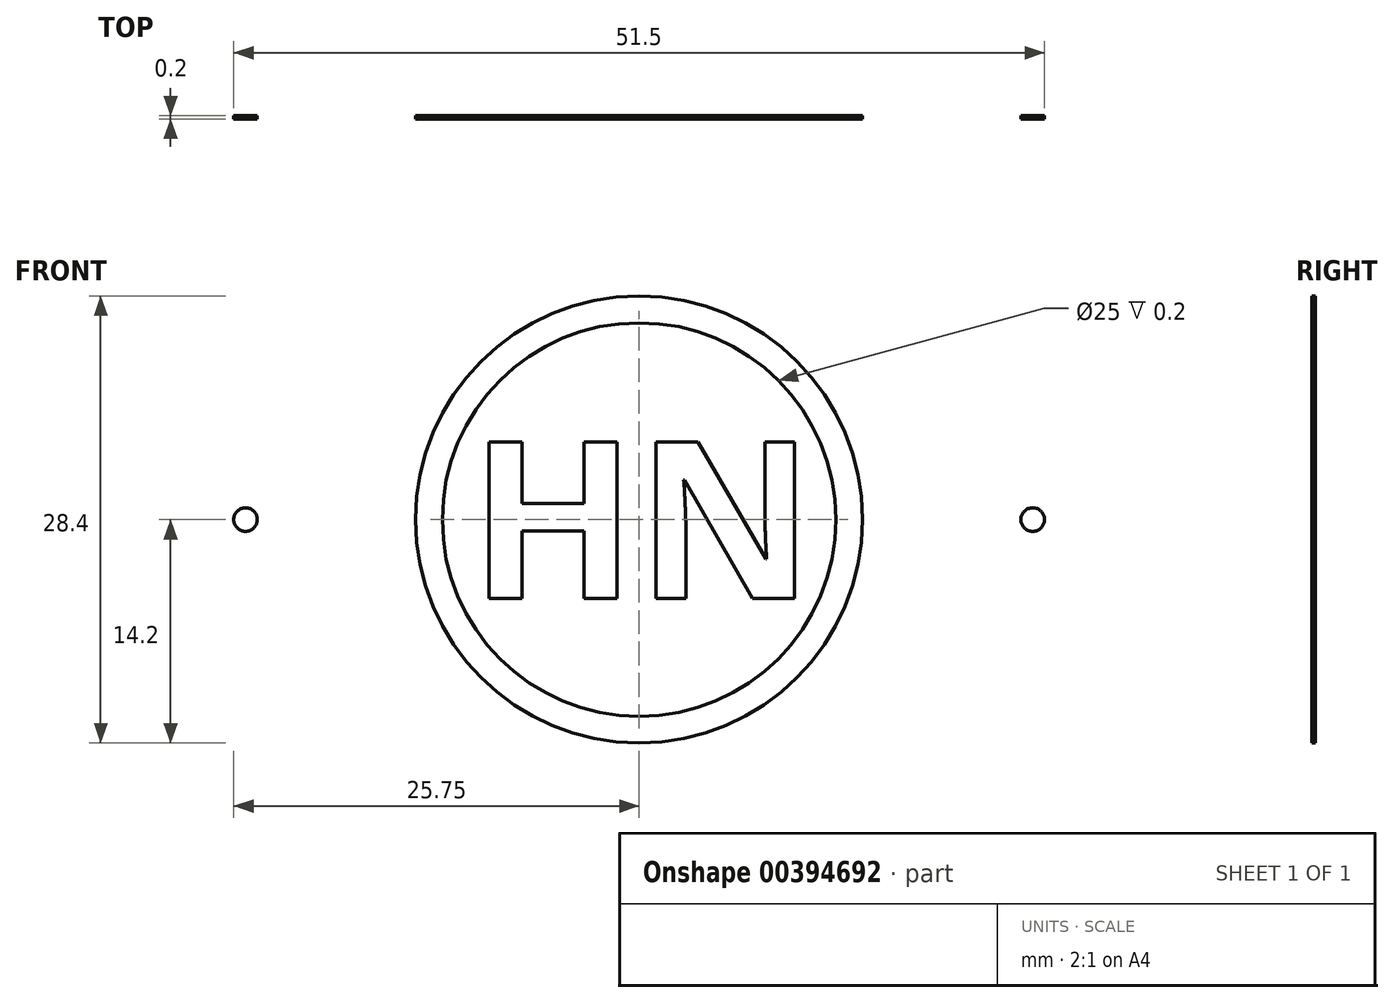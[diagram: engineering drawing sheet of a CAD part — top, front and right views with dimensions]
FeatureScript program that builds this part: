
annotation { "Feature Type Name" : "Feature", "Feature Type Description" : "" }
export const myFeature = defineFeature(function(context is Context, id is Id, definition is map)
    precondition{}
    {
        {
            var Q0;
            Q0=qCreatedBy(makeId("Front.planeOp"),FACE);
            var sketch = newSketch(context, id + "F0", { "sketchPlane" : qUnion([Q0])});
            skCircle(sketch, "E0", {"center": v(0, 0) * mm, "radius": 17.5 * mm});
            skSolve(sketch);
        }
        {
            var Q0;
            Q0=qSketchRegion(id+"F0",true);
            extrude(context, id + "F1", {"entities" : qUnion([Q0]), "depth" : 1 * mm});
        }
        {
            var Q0;
            Q0=makeQuery(id+"F1.opExtrude","CAP_FACE",FACE,{"disambiguationData":[OSD([sQuery(id+"F0.wireOp",EDGE,"E0")])],"isStart":true});
            var sketch = newSketch(context, id + "F2", { "sketchPlane" : qUnion([Q0])});
            skCircle(sketch, "E1", {"center": v(0, 0) * mm, "radius": 17.5 * mm});
            skCircle(sketch, "E2", {"center": v(0, 0) * mm, "radius": 15.25 * mm});
            skSolve(sketch);
        }
        {
            var Q0;
            Q0=qSketchRegion(id+"F2",true);
            extrude(context, id + "F3", {"entities" : qUnion([Q0]), "operationType" : NewBodyOperationType.ADD, "depth" : 1 * mm});
        }
        {
            var Q0;
            Q0=makeQuery(id+"F3.opExtrude","CAP_FACE",FACE,{"disambiguationData":[OSD([sQuery(id+"F2.wireOp",EDGE,"E1"),sQuery(id+"F2.wireOp",EDGE,"E2")])],"isStart":false});
            var sketch = newSketch(context, id + "F4", { "sketchPlane" : qUnion([Q0])});
            skCircle(sketch, "E3", {"center": v(0, 0) * mm, "radius": 17.5 * mm});
            skSolve(sketch);
        }
        {
            var Q0;
            Q0=qSketchRegion(id+"F4",true);
            extrude(context, id + "F5", {"entities" : qUnion([Q0]), "operationType" : NewBodyOperationType.ADD, "depth" : 1 * mm});
        }
        {
            var Q0;
            Q0=makeQuery(id+"F1.opExtrude","CAP_FACE",FACE,{"disambiguationData":[OSD([sQuery(id+"F0.wireOp",EDGE,"E0")])],"isStart":false});
            var sketch = newSketch(context, id + "F6", { "sketchPlane" : qUnion([Q0])});
            skText(sketch, "E4", { "text": "HN", "fontName": "OpenSans-Bold.ttf"});
            skCircle(sketch, "E5", {"center": v(0, 0) * mm, "radius": 12.5 * mm});
            skCircle(sketch, "E6", {"center": v(0, 0) * mm, "radius": 14.2 * mm});
            const initialGuessF6  = {"E4": [-0.01079, -0.005, 1, 0, 0.01]};
            skSetInitialGuess(sketch, initialGuessF6);
            skSolve(sketch);
        }
        {
            var Q0;
            Q0=makeQuery(id+"F6.imprint","IMPRINT",FACE,{"disambiguationData":[TD([[makeQuery(id+"F6.imprint","IMPRINT",EDGE,{"derivedFrom":sQuery(id+"F6.wireOp",EDGE,"E5")}),-1.0]])]});
            var Q1;
            Q1=makeQuery(id+"F6.imprint","IMPRINT",FACE,{"disambiguationData":[TD([[makeQuery(id+"F6.imprint","IMPRINT",EDGE,{"derivedFrom":sQuery(id+"F6.wireOp",EDGE,"E4.sketch_text.stroke-0")}),-1.0]])]});
            var Q2;
            Q2=makeQuery(id+"F6.imprint","IMPRINT",FACE,{"disambiguationData":[TD([[makeQuery(id+"F6.imprint","IMPRINT",EDGE,{"derivedFrom":sQuery(id+"F6.wireOp",EDGE,"E4.sketch_text.stroke-12")}),-1.0]])]});
            var Q3;
            Q3=makeQuery(id+"F6.imprint","IMPRINT",FACE,{"disambiguationData":[TD([[makeQuery(id+"F6.imprint","IMPRINT",EDGE,{"derivedFrom":sQuery(id+"F6.wireOp",EDGE,"E4.sketch_text.stroke-20")}),-1.0]])]});
            var Q4;
            Q4=makeQuery(id+"F6.imprint","IMPRINT",FACE,{"disambiguationData":[TD([[makeQuery(id+"F6.imprint","IMPRINT",EDGE,{"derivedFrom":sQuery(id+"F6.wireOp",EDGE,"E4.sketch_text.stroke-34")}),-1.0]])]});
            var Q5;
            Q5=makeQuery(id+"F6.imprint","IMPRINT",FACE,{"disambiguationData":[TD([[makeQuery(id+"F6.imprint","IMPRINT",EDGE,{"derivedFrom":sQuery(id+"F6.wireOp",EDGE,"2f791306-b3d7-45ab-86ae-8695a74e6aea.sketch_text.stroke-0")}),-1.0]])]});
            var Q6;
            Q6=makeQuery(id+"F6.imprint","IMPRINT",FACE,{"disambiguationData":[TD([[makeQuery(id+"F6.imprint","IMPRINT",EDGE,{"derivedFrom":sQuery(id+"F6.wireOp",EDGE,"2f791306-b3d7-45ab-86ae-8695a74e6aea.sketch_text.stroke-10")}),-1.0]])]});
            var Q7;
            Q7=makeQuery(id+"F6.imprint","IMPRINT",FACE,{"disambiguationData":[TD([[makeQuery(id+"F6.imprint","IMPRINT",EDGE,{"derivedFrom":sQuery(id+"F6.wireOp",EDGE,"2f791306-b3d7-45ab-86ae-8695a74e6aea.sketch_text.stroke-14")}),-1.0]])]});
            var Q8;
            Q8=makeQuery(id+"F6.imprint","IMPRINT",FACE,{"disambiguationData":[TD([[makeQuery(id+"F6.imprint","IMPRINT",EDGE,{"derivedFrom":sQuery(id+"F6.wireOp",EDGE,"2f791306-b3d7-45ab-86ae-8695a74e6aea.sketch_text.stroke-30")}),-1.0]])]});
            extrude(context, id + "F7", {"entities" : qUnion([Q0, Q1, Q2, Q3, Q4, Q5, Q6, Q7, Q8]), "operationType" : NewBodyOperationType.REMOVE, "oppositeDirection" : true, "depth" : 0.2 * mm});
        }
        {
            var Q0;
            Q0=makeQuery(id+"F7.boolean.opBoolean","COPY",FACE,{"derivedFrom":makeQuery(id+"F7.opExtrude","CAP_FACE",FACE,{"disambiguationData":[OSD([sQuery(id+"F6.wireOp",EDGE,"E5"),sQuery(id+"F6.wireOp",EDGE,"E6")])],"isStart":false})});
            var sketch = newSketch(context, id + "F8", { "sketchPlane" : qUnion([Q0])});
            skCircle(sketch, "E7", {"center": v(0, 0) * mm, "radius": 16.5 * mm});
            skCircle(sketch, "E8", {"center": v(0, 0) * mm, "radius": 15 * mm});
            skText(sketch, "E9", { "text": "VIP", "fontName": "OpenSans-Bold.ttf"});
            skText(sketch, "E10", { "text": "H.N.", "fontName": "OpenSans-Bold.ttf"});
            const initialGuessF8  = {"E9": [-0.00735, 0.0025, 1, 0, 0.0065], "E10": [-0.00973, -0.009, 1, 0, 0.0065]};
            skSetInitialGuess(sketch, initialGuessF8);
            skSolve(sketch);
        }
        {
            var Q0;
            Q0=makeQuery(id+"F8.imprint","IMPRINT",FACE,{"disambiguationData":[TD([[makeQuery(id+"F8.imprint","IMPRINT",EDGE,{"derivedFrom":sQuery(id+"F8.wireOp",EDGE,"E9.sketch_text.stroke-0")}),-1.0]])]});
            var Q1;
            Q1=makeQuery(id+"F8.imprint","IMPRINT",FACE,{"disambiguationData":[TD([[makeQuery(id+"F8.imprint","IMPRINT",EDGE,{"derivedFrom":sQuery(id+"F8.wireOp",EDGE,"E9.sketch_text.stroke-10")}),-1.0]])]});
            var Q2;
            Q2=makeQuery(id+"F8.imprint","IMPRINT",FACE,{"disambiguationData":[TD([[makeQuery(id+"F8.imprint","IMPRINT",EDGE,{"derivedFrom":sQuery(id+"F8.wireOp",EDGE,"E9.sketch_text.stroke-14")}),-1.0]])]});
            var Q3;
            Q3=makeQuery(id+"F8.imprint","IMPRINT",FACE,{"disambiguationData":[TD([[makeQuery(id+"F8.imprint","IMPRINT",EDGE,{"derivedFrom":sQuery(id+"F8.wireOp",EDGE,"E9.sketch_text.stroke-30")}),-1.0]])]});
            var Q4;
            Q4=makeQuery(id+"F8.imprint","IMPRINT",FACE,{"disambiguationData":[TD([[makeQuery(id+"F8.imprint","IMPRINT",EDGE,{"derivedFrom":sQuery(id+"F8.wireOp",EDGE,"E10.sketch_text.stroke-0")}),-1.0]])]});
            var Q5;
            Q5=makeQuery(id+"F8.imprint","IMPRINT",FACE,{"disambiguationData":[TD([[makeQuery(id+"F8.imprint","IMPRINT",EDGE,{"derivedFrom":sQuery(id+"F8.wireOp",EDGE,"E10.sketch_text.stroke-12")}),-1.0]])]});
            var Q6;
            Q6=makeQuery(id+"F8.imprint","IMPRINT",FACE,{"disambiguationData":[TD([[makeQuery(id+"F8.imprint","IMPRINT",EDGE,{"derivedFrom":sQuery(id+"F8.wireOp",EDGE,"E10.sketch_text.stroke-20")}),-1.0]])]});
            var Q7;
            Q7=makeQuery(id+"F8.imprint","IMPRINT",FACE,{"disambiguationData":[TD([[makeQuery(id+"F8.imprint","IMPRINT",EDGE,{"derivedFrom":sQuery(id+"F8.wireOp",EDGE,"E10.sketch_text.stroke-34")}),-1.0]])]});
            var Q8;
            Q8=makeQuery(id+"F8.imprint","IMPRINT",FACE,{"disambiguationData":[TD([[makeQuery(id+"F8.imprint","IMPRINT",EDGE,{"derivedFrom":sQuery(id+"F8.wireOp",EDGE,"E7")}),1.0]])]});
            extrude(context, id + "F9", {"entities" : qUnion([Q0, Q1, Q2, Q3, Q4, Q5, Q6, Q7, Q8]), "depth" : 0.2 * mm});
        }
        {
            var Q0;
            Q0=makeQuery(id+"Fh8yMcBjIkPt4Dr_11.boolean.opBoolean","MERGE",FACE,{"derivedFrom":[makeQuery(id+"F5.opExtrude","CAP_FACE",FACE,{"disambiguationData":[OSD([sQuery(id+"F4.wireOp",EDGE,"E3")])],"isStart":false}),makeQuery(id+"Fh8yMcBjIkPt4Dr_11.opExtrude","CAP_FACE",FACE,{"disambiguationData":[OSD([sQuery(id+"FN8h1bw3wlibMYA_11.wireOp",EDGE,"BS7OUwbq-2ru2-1JD7-GIha-xYvTOZTgPK9A"),sQuery(id+"FN8h1bw3wlibMYA_11.wireOp",EDGE,"aJaIA7Kc-m8c6-AEcG-Va6J-VanrhZFaR41i")])],"isStart":false})]});
            var sketch = newSketch(context, id + "F10", { "sketchPlane" : qUnion([Q0])});
            skArc(sketch, "E11", {"start": v(12.63, -6.5) * mm, "mid": v(14.2, -0.52) * mm, "end": v(13.07, 5.55) * mm});
            skLineSegment(sketch, "E12", {"start": v(12.63, -6.5) * mm, "end": v(-4.7, 4) * mm});
            skLineSegment(sketch, "E13", {"start": v(-4.7, 4) * mm, "end": v(-4.7, 2.5) * mm});
            skLineSegment(sketch, "E14", {"start": v(-4.7, 2.5) * mm, "end": v(12.49, -6.76) * mm});
            skLineSegment(sketch, "E15", {"start": v(-4.7, 1.9) * mm, "end": v(-4.7, 0.4) * mm});
            skLineSegment(sketch, "E16", {"start": v(-4.7, 0.4) * mm, "end": v(11.53, -8.28) * mm});
            skLineSegment(sketch, "E17", {"start": v(11.7, -8.04) * mm, "end": v(-4.7, 1.9) * mm});
            skLineSegment(sketch, "E18", {"start": v(-4.7, -0.2) * mm, "end": v(-4.7, -1.7) * mm});
            skLineSegment(sketch, "E19", {"start": v(-4.7, -1.7) * mm, "end": v(10.39, -9.68) * mm});
            skLineSegment(sketch, "E20", {"start": v(10.6, -9.46) * mm, "end": v(-4.7, -0.2) * mm});
            skLineSegment(sketch, "E21", {"start": v(-4.7, -2.3) * mm, "end": v(-4.7, -3.8) * mm});
            skLineSegment(sketch, "E22", {"start": v(-4.7, -3.8) * mm, "end": v(9.04, -10.95) * mm});
            skLineSegment(sketch, "E23", {"start": v(9.27, -10.76) * mm, "end": v(-4.7, -2.3) * mm});
            skLineSegment(sketch, "E24", {"start": v(-4.7, -4.4) * mm, "end": v(-4.7, -5.9) * mm});
            skLineSegment(sketch, "E25", {"start": v(-4.7, -5.9) * mm, "end": v(7.46, -12.08) * mm});
            skLineSegment(sketch, "E26", {"start": v(7.72, -11.92) * mm, "end": v(-4.7, -4.4) * mm});
            skArc(sketch, "E27.trimOffspring", {"start": v(11.7, -8.04) * mm, "mid": v(12.11, -7.4) * mm, "end": v(12.49, -6.76) * mm});
            skArc(sketch, "E28.trimOffspring", {"start": v(10.6, -9.46) * mm, "mid": v(11.08, -8.88) * mm, "end": v(11.53, -8.28) * mm});
            skArc(sketch, "E29.trimOffspring", {"start": v(9.27, -10.76) * mm, "mid": v(9.84, -10.24) * mm, "end": v(10.39, -9.68) * mm});
            skArc(sketch, "E30.trimOffspring", {"start": v(7.72, -11.92) * mm, "mid": v(8.4, -11.46) * mm, "end": v(9.04, -10.95) * mm});
            skLineSegment(sketch, "E31", {"start": v(7.07, 12.32) * mm, "end": v(-4.2, 4.28) * mm});
            skLineSegment(sketch, "E32", {"start": v(-4.2, 4.28) * mm, "end": v(8.2, 11.59) * mm});
            skLineSegment(sketch, "E33", {"start": v(8.69, 11.23) * mm, "end": v(-2.5, 3.25) * mm});
            skLineSegment(sketch, "E34", {"start": v(-2.5, 3.25) * mm, "end": v(9.66, 10.4) * mm});
            skLineSegment(sketch, "E35", {"start": v(10.1, 10) * mm, "end": v(-0.8, 2.22) * mm});
            skLineSegment(sketch, "E36", {"start": v(11.3, 8.6) * mm, "end": v(0.9, 1.2) * mm});
            skLineSegment(sketch, "E37", {"start": v(0.9, 1.2) * mm, "end": v(12, 7.6) * mm});
            skLineSegment(sketch, "E38", {"start": v(12.3, 7.09) * mm, "end": v(2.6, 0.16) * mm});
            skLineSegment(sketch, "E39", {"start": v(2.6, 0.16) * mm, "end": v(13.07, 5.55) * mm});
            skArc(sketch, "E40.trimOffspring", {"start": v(7.07, 12.32) * mm, "mid": v(-14.2, -0.23) * mm, "end": v(7.46, -12.08) * mm});
            skArc(sketch, "E41.trimOffspring", {"start": v(8.69, 11.23) * mm, "mid": v(8.45, 11.41) * mm, "end": v(8.2, 11.59) * mm});
            skArc(sketch, "E42.trimOffspring", {"start": v(10.1, 10) * mm, "mid": v(9.88, 10.2) * mm, "end": v(9.66, 10.4) * mm});
            skArc(sketch, "E43.trimOffspring", {"start": v(11.3, 8.6) * mm, "mid": v(11.1, 8.84) * mm, "end": v(10.92, 9.08) * mm});
            skArc(sketch, "E44.trimOffspring", {"start": v(12.3, 7.09) * mm, "mid": v(12.15, 7.34) * mm, "end": v(12, 7.6) * mm});
            skLineSegment(sketch, "E45", {"start": v(10.92, 9.08) * mm, "end": v(-0.8, 2.22) * mm});
            skSolve(sketch);
        }
        {
            var Q0;
            Q0=qSketchRegion(id+"F10",true);
            extrude(context, id + "F11", {"entities" : qUnion([Q0]), "operationType" : NewBodyOperationType.ADD, "depth" : 0.4 * mm});
        }
        {
            var Q0;
            Q0=makeQuery(id+"F9.opExtrude","SWEPT_BODY",BODY,{"disambiguationData":[OSD([sQuery(id+"F8.wireOp",EDGE,"E7"),sQuery(id+"F8.wireOp",EDGE,"E8")])]});
            var Q1;
            Q1=makeQuery(id+"F9.opExtrude","SWEPT_BODY",BODY,{"disambiguationData":[OSD([sQuery(id+"F8.wireOp",EDGE,"E9.sketch_text.stroke-0"),sQuery(id+"F8.wireOp",EDGE,"E9.sketch_text.stroke-1"),sQuery(id+"F8.wireOp",EDGE,"E9.sketch_text.stroke-2"),sQuery(id+"F8.wireOp",EDGE,"E9.sketch_text.stroke-3"),sQuery(id+"F8.wireOp",EDGE,"E9.sketch_text.stroke-4"),sQuery(id+"F8.wireOp",EDGE,"E9.sketch_text.stroke-5"),sQuery(id+"F8.wireOp",EDGE,"E9.sketch_text.stroke-6"),sQuery(id+"F8.wireOp",EDGE,"E9.sketch_text.stroke-7"),sQuery(id+"F8.wireOp",EDGE,"E9.sketch_text.stroke-8"),sQuery(id+"F8.wireOp",EDGE,"E9.sketch_text.stroke-9")])]});
            var Q2;
            Q2=makeQuery(id+"F9.opExtrude","SWEPT_BODY",BODY,{"disambiguationData":[OSD([sQuery(id+"F8.wireOp",EDGE,"E9.sketch_text.stroke-14"),sQuery(id+"F8.wireOp",EDGE,"E9.sketch_text.stroke-15"),sQuery(id+"F8.wireOp",EDGE,"E9.sketch_text.stroke-16"),sQuery(id+"F8.wireOp",EDGE,"E9.sketch_text.stroke-17"),sQuery(id+"F8.wireOp",EDGE,"E9.sketch_text.stroke-18"),sQuery(id+"F8.wireOp",EDGE,"E9.sketch_text.stroke-19"),sQuery(id+"F8.wireOp",EDGE,"E9.sketch_text.stroke-20"),sQuery(id+"F8.wireOp",EDGE,"E9.sketch_text.stroke-21"),sQuery(id+"F8.wireOp",EDGE,"E9.sketch_text.stroke-22"),sQuery(id+"F8.wireOp",EDGE,"E9.sketch_text.stroke-23"),sQuery(id+"F8.wireOp",EDGE,"E9.sketch_text.stroke-24"),sQuery(id+"F8.wireOp",EDGE,"E9.sketch_text.stroke-25"),sQuery(id+"F8.wireOp",EDGE,"E9.sketch_text.stroke-26"),sQuery(id+"F8.wireOp",EDGE,"E9.sketch_text.stroke-27"),sQuery(id+"F8.wireOp",EDGE,"E9.sketch_text.stroke-28"),sQuery(id+"F8.wireOp",EDGE,"E9.sketch_text.stroke-29")])]});
            var Q3;
            Q3=makeQuery(id+"F9.opExtrude","SWEPT_BODY",BODY,{"disambiguationData":[OSD([sQuery(id+"F8.wireOp",EDGE,"E10.sketch_text.stroke-34"),sQuery(id+"F8.wireOp",EDGE,"E10.sketch_text.stroke-35"),sQuery(id+"F8.wireOp",EDGE,"E10.sketch_text.stroke-36"),sQuery(id+"F8.wireOp",EDGE,"E10.sketch_text.stroke-37"),sQuery(id+"F8.wireOp",EDGE,"E10.sketch_text.stroke-38"),sQuery(id+"F8.wireOp",EDGE,"E10.sketch_text.stroke-39"),sQuery(id+"F8.wireOp",EDGE,"E10.sketch_text.stroke-40"),sQuery(id+"F8.wireOp",EDGE,"E10.sketch_text.stroke-41")])]});
            var Q4;
            Q4=makeQuery(id+"F9.opExtrude","SWEPT_BODY",BODY,{"disambiguationData":[OSD([sQuery(id+"F8.wireOp",EDGE,"E10.sketch_text.stroke-0"),sQuery(id+"F8.wireOp",EDGE,"E10.sketch_text.stroke-1"),sQuery(id+"F8.wireOp",EDGE,"E10.sketch_text.stroke-2"),sQuery(id+"F8.wireOp",EDGE,"E10.sketch_text.stroke-3"),sQuery(id+"F8.wireOp",EDGE,"E10.sketch_text.stroke-4"),sQuery(id+"F8.wireOp",EDGE,"E10.sketch_text.stroke-5"),sQuery(id+"F8.wireOp",EDGE,"E10.sketch_text.stroke-6"),sQuery(id+"F8.wireOp",EDGE,"E10.sketch_text.stroke-7"),sQuery(id+"F8.wireOp",EDGE,"E10.sketch_text.stroke-8"),sQuery(id+"F8.wireOp",EDGE,"E10.sketch_text.stroke-9"),sQuery(id+"F8.wireOp",EDGE,"E10.sketch_text.stroke-10"),sQuery(id+"F8.wireOp",EDGE,"E10.sketch_text.stroke-11")])]});
            deleteBodies(context, id + "F12", {"entities" : qUnion([Q0, Q1, Q2, Q3, Q4])});
        }
        {
            var Q0;
            Q0=makeQuery(id+"F9.opExtrude","SWEPT_BODY",BODY,{"disambiguationData":[OSD([sQuery(id+"F8.wireOp",EDGE,"E9.sketch_text.stroke-10"),sQuery(id+"F8.wireOp",EDGE,"E9.sketch_text.stroke-11"),sQuery(id+"F8.wireOp",EDGE,"E9.sketch_text.stroke-12"),sQuery(id+"F8.wireOp",EDGE,"E9.sketch_text.stroke-13")])]});
            var Q1;
            Q1=makeQuery(id+"F9.opExtrude","SWEPT_BODY",BODY,{"disambiguationData":[OSD([sQuery(id+"F8.wireOp",EDGE,"E10.sketch_text.stroke-12"),sQuery(id+"F8.wireOp",EDGE,"E10.sketch_text.stroke-13"),sQuery(id+"F8.wireOp",EDGE,"E10.sketch_text.stroke-14"),sQuery(id+"F8.wireOp",EDGE,"E10.sketch_text.stroke-15"),sQuery(id+"F8.wireOp",EDGE,"E10.sketch_text.stroke-16"),sQuery(id+"F8.wireOp",EDGE,"E10.sketch_text.stroke-17"),sQuery(id+"F8.wireOp",EDGE,"E10.sketch_text.stroke-18"),sQuery(id+"F8.wireOp",EDGE,"E10.sketch_text.stroke-19")])]});
            deleteBodies(context, id + "F13", {"entities" : qUnion([Q0, Q1])});
        }
        {
            var Q0;
            Q0=makeQuery(id+"F9.opExtrude","SWEPT_BODY",BODY,{"disambiguationData":[OSD([sQuery(id+"F8.wireOp",EDGE,"E10.sketch_text.stroke-20"),sQuery(id+"F8.wireOp",EDGE,"E10.sketch_text.stroke-21"),sQuery(id+"F8.wireOp",EDGE,"E10.sketch_text.stroke-22"),sQuery(id+"F8.wireOp",EDGE,"E10.sketch_text.stroke-23"),sQuery(id+"F8.wireOp",EDGE,"E10.sketch_text.stroke-24"),sQuery(id+"F8.wireOp",EDGE,"E10.sketch_text.stroke-25"),sQuery(id+"F8.wireOp",EDGE,"E10.sketch_text.stroke-26"),sQuery(id+"F8.wireOp",EDGE,"E10.sketch_text.stroke-27"),sQuery(id+"F8.wireOp",EDGE,"E10.sketch_text.stroke-28"),sQuery(id+"F8.wireOp",EDGE,"E10.sketch_text.stroke-29"),sQuery(id+"F8.wireOp",EDGE,"E10.sketch_text.stroke-30"),sQuery(id+"F8.wireOp",EDGE,"E10.sketch_text.stroke-31"),sQuery(id+"F8.wireOp",EDGE,"E10.sketch_text.stroke-32"),sQuery(id+"F8.wireOp",EDGE,"E10.sketch_text.stroke-33")])]});
            deleteBodies(context, id + "F14", {"entities" : qUnion([Q0])});
        }
        {
            var Q0;
            {var subQ0=sQuery(id+"F0.wireOp",EDGE,"E0");Q0=makeQuery(id+"F7.boolean.opBoolean","SPLIT",FACE,{"disambiguationData":[TD([makeQuery(id+"F1.opExtrude","SWEPT_FACE",FACE,{"disambiguationData":[OSD([subQ0])]})])],"derivedFrom":makeQuery(id+"F1.opExtrude","CAP_FACE",FACE,{"disambiguationData":[OSD([subQ0])],"isStart":false})});}
            var sketch = newSketch(context, id + "F15", { "sketchPlane" : qUnion([Q0])});
            skCircle(sketch, "E46", {"center": v(0, 19.5) * mm, "radius": 2 * mm});
            skCircle(sketch, "E47", {"center": v(0, 19.5) * mm, "radius": 4 * mm});
            skSolve(sketch);
        }
        {
            var Q0;
            Q0=qSketchRegion(id+"F15",true);
            var Q1;
            Q1=makeQuery(id+"F5.opExtrude","CAP_FACE",FACE,{"disambiguationData":[OSD([sQuery(id+"F4.wireOp",EDGE,"E3")])],"isStart":false});
            extrude(context, id + "F16", {"entities" : qUnion([Q0]), "operationType" : NewBodyOperationType.ADD, "endBound" : BoundingType.UP_TO_SURFACE, "oppositeDirection" : true, "endBoundEntityFace" : qUnion([Q1]), "depth" : 25 * mm});
        }
        {
            var Q0;
            Q0=makeQuery(id+"F16.boolean.opBoolean","INTERSECT",EDGE,{"disambiguationData":[OD(0.0)],"derivedFrom":[makeQuery(id+"F5.boolean.opBoolean","MERGE",FACE,{"derivedFrom":[makeQuery(id+"F3.boolean.opBoolean","MERGE",FACE,{"derivedFrom":[makeQuery(id+"F1.opExtrude","SWEPT_FACE",FACE,{"disambiguationData":[OSD([sQuery(id+"F0.wireOp",EDGE,"E0")])]}),makeQuery(id+"F3.opExtrude","SWEPT_FACE",FACE,{"disambiguationData":[OSD([sQuery(id+"F2.wireOp",EDGE,"E1")])]})]}),makeQuery(id+"F5.opExtrude","SWEPT_FACE",FACE,{"disambiguationData":[OSD([sQuery(id+"F4.wireOp",EDGE,"E3")])]})]}),makeQuery(id+"F16.opExtrude","SWEPT_FACE",FACE,{"disambiguationData":[OSD([sQuery(id+"F15.wireOp",EDGE,"E47")])]})]});
            var Q1;
            Q1=makeQuery(id+"F16.boolean.opBoolean","INTERSECT",EDGE,{"disambiguationData":[OD(1.0)],"derivedFrom":[makeQuery(id+"F5.boolean.opBoolean","MERGE",FACE,{"derivedFrom":[makeQuery(id+"F3.boolean.opBoolean","MERGE",FACE,{"derivedFrom":[makeQuery(id+"F1.opExtrude","SWEPT_FACE",FACE,{"disambiguationData":[OSD([sQuery(id+"F0.wireOp",EDGE,"E0")])]}),makeQuery(id+"F3.opExtrude","SWEPT_FACE",FACE,{"disambiguationData":[OSD([sQuery(id+"F2.wireOp",EDGE,"E1")])]})]}),makeQuery(id+"F5.opExtrude","SWEPT_FACE",FACE,{"disambiguationData":[OSD([sQuery(id+"F4.wireOp",EDGE,"E3")])]})]}),makeQuery(id+"F16.opExtrude","SWEPT_FACE",FACE,{"disambiguationData":[OSD([sQuery(id+"F15.wireOp",EDGE,"E47")])]})]});
            fillet(context, id + "F17", {"entities" : qUnion([Q0, Q1]), "radius" : 5 * mm, "tangentPropagation" : true, "allowEdgeOverflow" : false});
        }
        {
            var Q0;
            Q0=makeQuery(id+"F1.opExtrude","CAP_EDGE",EDGE,{"disambiguationData":[OSD([sQuery(id+"F0.wireOp",EDGE,"E0")])],"isStart":false});
            var Q1;
            {var subQ0=sQuery(id+"F15.wireOp",EDGE,"E47");var subQ1=sQuery(id+"F4.wireOp",EDGE,"E3");Q1=makeQuery(id+"F17.opFillet","BLEND_EDGE",EDGE,{"blendedFrom":[makeQuery(id+"F16.boolean.opBoolean","INTERSECT",EDGE,{"disambiguationData":[OD(0.0)],"derivedFrom":[makeQuery(id+"F5.boolean.opBoolean","MERGE",FACE,{"derivedFrom":[makeQuery(id+"F3.boolean.opBoolean","MERGE",FACE,{"derivedFrom":[makeQuery(id+"F1.opExtrude","SWEPT_FACE",FACE,{"disambiguationData":[OSD([sQuery(id+"F0.wireOp",EDGE,"E0")])]}),makeQuery(id+"F3.opExtrude","SWEPT_FACE",FACE,{"disambiguationData":[OSD([sQuery(id+"F2.wireOp",EDGE,"E1")])]})]}),makeQuery(id+"F5.opExtrude","SWEPT_FACE",FACE,{"disambiguationData":[OSD([subQ1])]})]}),makeQuery(id+"F16.opExtrude","SWEPT_FACE",FACE,{"disambiguationData":[OSD([subQ0])]})]}),makeQuery(id+"F16.boolean.opBoolean","MERGE",FACE,{"derivedFrom":[makeQuery(id+"F5.opExtrude","CAP_FACE",FACE,{"disambiguationData":[OSD([subQ1])],"isStart":false}),makeQuery(id+"F16.opExtrude","CAP_FACE",FACE,{"disambiguationData":[OSD([sQuery(id+"F15.wireOp",EDGE,"E46"),subQ0])],"isStart":false})]})],"blendedInto":[makeQuery(id+"F16.boolean.opBoolean","MERGE",FACE,{"derivedFrom":[makeQuery(id+"F5.opExtrude","CAP_FACE",FACE,{"disambiguationData":[OSD([subQ1])],"isStart":false}),makeQuery(id+"F16.opExtrude","CAP_FACE",FACE,{"disambiguationData":[OSD([sQuery(id+"F15.wireOp",EDGE,"E46"),subQ0])],"isStart":false})]})]});}
            var Q2;
            Q2=makeQuery(id+"F16.opExtrude","CAP_EDGE",EDGE,{"disambiguationData":[OSD([sQuery(id+"F15.wireOp",EDGE,"E46")])],"isStart":true});
            var Q3;
            Q3=makeQuery(id+"F16.opExtrude","CAP_EDGE",EDGE,{"disambiguationData":[OSD([sQuery(id+"F15.wireOp",EDGE,"E46")])],"isStart":false});
            fillet(context, id + "F18", {"entities" : qUnion([Q0, Q1, Q2, Q3]), "radius" : 1.5 * mm, "tangentPropagation" : true, "allowEdgeOverflow" : false});
        }
        {
            var Q0;
            {var subQ0=sQuery(id+"F0.wireOp",EDGE,"E0");Q0=makeQuery(id+"F16.boolean.opBoolean","MERGE",FACE,{"derivedFrom":[makeQuery(id+"F7.boolean.opBoolean","SPLIT",FACE,{"disambiguationData":[TD([makeQuery(id+"F1.opExtrude","SWEPT_FACE",FACE,{"disambiguationData":[OSD([subQ0])]})])],"derivedFrom":makeQuery(id+"F1.opExtrude","CAP_FACE",FACE,{"disambiguationData":[OSD([subQ0])],"isStart":false})}),makeQuery(id+"F16.opExtrude","CAP_FACE",FACE,{"disambiguationData":[OSD([sQuery(id+"F15.wireOp",EDGE,"E46"),sQuery(id+"F15.wireOp",EDGE,"E47")])],"isStart":true})]});}
            var sketch = newSketch(context, id + "F19", { "sketchPlane" : qUnion([Q0])});
            skCircle(sketch, "E48", {"center": v(25, 0) * mm, "radius": 0.75 * mm});
            skCircle(sketch, "E49", {"center": v(-25, 0) * mm, "radius": 0.75 * mm});
            skSolve(sketch);
        }
        {
            var Q0;
            Q0=qSketchRegion(id+"F19",true);
            extrude(context, id + "F20", {"entities" : qUnion([Q0]), "oppositeDirection" : true, "depth" : 0.2 * mm});
        }
        {
            var Q0;
            {var subQ0=sQuery(id+"F0.wireOp",EDGE,"E0");Q0=makeQuery(id+"F16.boolean.opBoolean","MERGE",FACE,{"derivedFrom":[makeQuery(id+"F7.boolean.opBoolean","SPLIT",FACE,{"disambiguationData":[TD([makeQuery(id+"F1.opExtrude","SWEPT_FACE",FACE,{"disambiguationData":[OSD([subQ0])]})])],"derivedFrom":makeQuery(id+"F1.opExtrude","CAP_FACE",FACE,{"disambiguationData":[OSD([subQ0])],"isStart":false})}),makeQuery(id+"F16.opExtrude","CAP_FACE",FACE,{"disambiguationData":[OSD([sQuery(id+"F15.wireOp",EDGE,"E46"),sQuery(id+"F15.wireOp",EDGE,"E47")])],"isStart":true})]});}
            var sketch = newSketch(context, id + "F21", { "sketchPlane" : qUnion([Q0])});
            skCircle(sketch, "E50", {"center": v(0, 0) * mm, "radius": 14.2 * mm});
            skCircle(sketch, "E51", {"center": v(0, 0) * mm, "radius": 12.5 * mm});
            skText(sketch, "E52", { "text": "HN", "fontName": "OpenSans-Bold.ttf"});
            const initialGuessF21  = {"E52": [-0.01079, -0.005, 1, 0, 0.01]};
            skSetInitialGuess(sketch, initialGuessF21);
            skSolve(sketch);
        }
        {
            var Q0;
            Q0=makeQuery(id+"F21.imprint","IMPRINT",FACE,{"disambiguationData":[TD([[makeQuery(id+"F21.imprint","IMPRINT",EDGE,{"derivedFrom":sQuery(id+"F21.wireOp",EDGE,"E50")}),1.0]])]});
            var Q1;
            Q1=makeQuery(id+"F21.imprint","IMPRINT",FACE,{"disambiguationData":[TD([[makeQuery(id+"F21.imprint","IMPRINT",EDGE,{"derivedFrom":sQuery(id+"F21.wireOp",EDGE,"E52.sketch_text.stroke-0")}),-1.0]])]});
            var Q2;
            Q2=makeQuery(id+"F21.imprint","IMPRINT",FACE,{"disambiguationData":[TD([[makeQuery(id+"F21.imprint","IMPRINT",EDGE,{"derivedFrom":sQuery(id+"F21.wireOp",EDGE,"E52.sketch_text.stroke-12")}),-1.0]])]});
            extrude(context, id + "F22", {"entities" : qUnion([Q0, Q1, Q2]), "oppositeDirection" : true, "depth" : 0.2 * mm});
        }
        {
            var Q0;
            Q0=makeQuery(id+"F1.opExtrude","SWEPT_BODY",BODY,{"disambiguationData":[OSD([sQuery(id+"F0.wireOp",EDGE,"E0")])]});
            deleteBodies(context, id + "F23", {"entities" : qUnion([Q0])});
        }
    });
